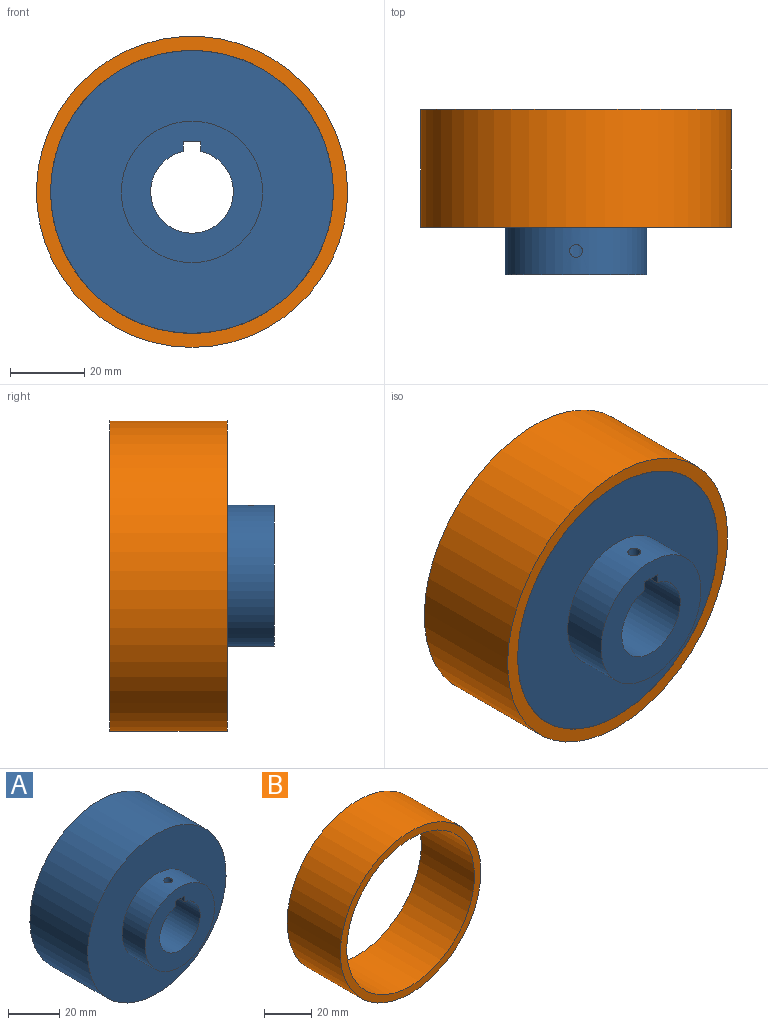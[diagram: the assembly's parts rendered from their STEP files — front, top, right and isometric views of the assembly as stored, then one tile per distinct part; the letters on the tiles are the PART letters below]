
ASSEMBLY  parts=2 mates=1
PART A: 10 faces, bbox 76.2x44.5x76.2 mm
  f0: cylinder r=19.05mm len=38.1mm, axis (0,1,0), area 1510.8mm2, adj f2,f5,f9
  f1: cylinder r=11.13mm len=44.45mm, axis (0,1,0), area 2893.8mm2, adj f2,f3,f6,f8
  f2: plane 38.1x38.1mm, normal (0,-1,0), area 739.5mm2, adj f0,f1,f6,f7,f8
  f3: plane 76.2x76.2mm, normal (0,1,0), area 4159.8mm2, adj f1,f4,f6,f7,f8
  f4: cylinder r=38.1mm len=76.2mm, axis (0,-1,0), area 7600.6mm2, adj f3,f5
  f5: plane 76.2x76.2mm, normal (0,-1,0), area 3420.3mm2, adj f0,f4
  f6: plane 44.45x2.64mm, normal (-1,0,0), area 117.3mm2, adj f1,f2,f3,f7
  f7: plane 44.45x4.76mm, normal (0,0,-1), area 202.3mm2, adj f2,f3,f6,f8,f9
  f8: plane 44.45x2.64mm, normal (1,0,0), area 117.3mm2, adj f1,f2,f3,f7
  f9: cylinder r=1.73mm len=5.54mm, axis (0,0,1), area 59.7mm2, adj f0,f7
PART B: 4 faces, bbox 83.8x31.8x83.8 mm
  f0: cylinder r=38.1mm len=76.2mm, axis (0,1,0), area 7600.6mm2, adj f2,f3
  f1: cylinder r=41.91mm len=83.82mm, axis (0,1,0), area 8360.7mm2, adj f2,f3
  f2: plane 83.82x83.82mm, normal (0,-1,0), area 957.7mm2, adj f0,f1
  f3: plane 83.82x83.82mm, normal (0,1,0), area 957.7mm2, adj f0,f1
PLACE A t=(-5.53,-17.94,-0.7)mm
PLACE B t=(-5.53,13.81,-0.7)mm
MATE fastened B.f0 <-> A.f4  axis (0,1,0) through (-5.53,13.81,-0.7)mm
